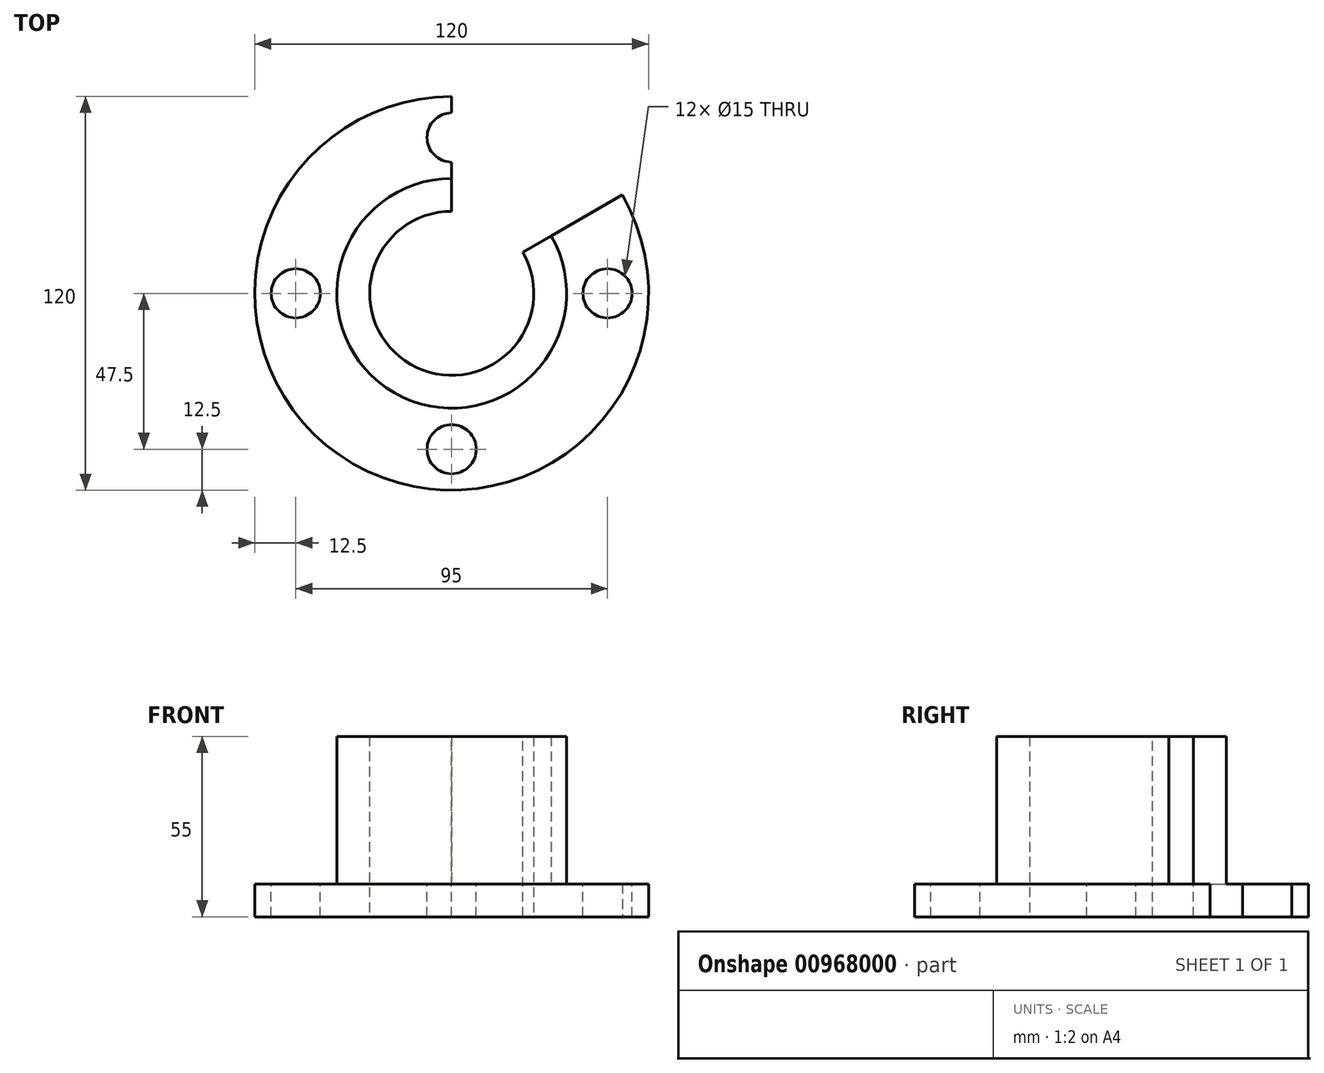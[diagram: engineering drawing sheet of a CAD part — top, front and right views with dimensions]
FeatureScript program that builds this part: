
annotation { "Feature Type Name" : "Feature", "Feature Type Description" : "" }
export const myFeature = defineFeature(function(context is Context, id is Id, definition is map)
    precondition{}
    {
        {
            var Q0;
            Q0=qCreatedBy(makeId("Right.planeOp"),FACE);
            var sketch = newSketch(context, id + "F0", { "sketchPlane" : qUnion([Q0])});
            skLineSegment(sketch, "E0", {"start": v(0, 0) * mm, "end": v(0, 50.5) * mm});
            skLineSegment(sketch, "E1", {"start": v(25, 0) * mm, "end": v(25, 55) * mm});
            skLineSegment(sketch, "E2", {"start": v(25, 55) * mm, "end": v(35, 55) * mm});
            skLineSegment(sketch, "E3", {"start": v(35, 55) * mm, "end": v(35, 10) * mm});
            skLineSegment(sketch, "E4", {"start": v(35, 10) * mm, "end": v(60, 10) * mm});
            skLineSegment(sketch, "E5", {"start": v(60, 10) * mm, "end": v(60, 0) * mm});
            skLineSegment(sketch, "E6", {"start": v(60, 0) * mm, "end": v(25, 0) * mm});
            skSolve(sketch);
        }
        {
            var Q0;
            Q0 = qSketchRegion(id + "F0", true);
            var Q1;
            Q1=sQuery(id+"F0.wireOp",EDGE,"E0");
            revolve(context, id + "F1", {"surfaceOperationType" : NewSurfaceOperationType.NEW, "entities" : qUnion([Q0]), "axis" : qUnion([Q1]), "revolveType" : RevolveType.ONE_DIRECTION, "angle" : 300 * degree});
        }
        {
            var Q0;
            Q0=makeQuery(id+"F1.opRevolve","SWEPT_FACE",FACE,{"disambiguationData":[OSD([sQuery(id+"F0.wireOp",EDGE,"E4")])]});
            var sketch = newSketch(context, id + "F2", { "sketchPlane" : qUnion([Q0])});
            skCircle(sketch, "E7", {"center": v(-47.5, 0) * mm, "radius": 7.5 * mm});
            skCircle(sketch, "E8", {"center": v(47.5, 0) * mm, "radius": 7.5 * mm});
            skCircle(sketch, "E9", {"center": v(0, 47.5) * mm, "radius": 7.5 * mm});
            skCircle(sketch, "E10", {"center": v(0, -47.5) * mm, "radius": 7.5 * mm});
            skSolve(sketch);
        }
        {
            var Q0;
            Q0=makeQuery(id+"F2.imprint","IMPRINT",FACE,{"disambiguationData":[TD([[makeQuery(id+"F2.imprint","IMPRINT",EDGE,{"derivedFrom":sQuery(id+"F2.wireOp",EDGE,"E7")}),1.0]])]});
            var Q1;
            Q1=makeQuery(id+"F2.imprint","IMPRINT",FACE,{"disambiguationData":[TD([[makeQuery(id+"F2.imprint","IMPRINT",EDGE,{"derivedFrom":sQuery(id+"F2.wireOp",EDGE,"E8")}),1.0]])]});
            var Q2;
            {var subQ0=sQuery(id+"F2.wireOp",EDGE,"E9");var subQ1=makeQuery(id+"F1.opRevolve","CAP_EDGE",EDGE,{"disambiguationData":[OSD([sQuery(id+"F0.wireOp",EDGE,"E4")])],"isStart":true});var subQ2=makeQuery(id+"F2.imprint","INTERSECT",VERTEX,{"disambiguationData":[OD(0.0)],"derivedFrom":[subQ1,subQ0]});Q2=makeQuery(id+"F2.imprint","IMPRINT",FACE,{"disambiguationData":[TD([[makeQuery(id+"F2.imprint","IMPRINT",EDGE,{"disambiguationData":[TD([[subQ2,-1.0]])],"derivedFrom":subQ0}),1.0]])]});}
            var Q3;
            {var subQ0=sQuery(id+"F2.wireOp",EDGE,"E9");var subQ1=makeQuery(id+"F1.opRevolve","CAP_EDGE",EDGE,{"disambiguationData":[OSD([sQuery(id+"F0.wireOp",EDGE,"E4")])],"isStart":true});var subQ2=makeQuery(id+"F2.imprint","INTERSECT",VERTEX,{"disambiguationData":[OD(0.0)],"derivedFrom":[subQ1,subQ0]});Q3=makeQuery(id+"F2.imprint","IMPRINT",FACE,{"disambiguationData":[TD([[makeQuery(id+"F2.imprint","IMPRINT",EDGE,{"disambiguationData":[TD([[subQ2,1.0]])],"derivedFrom":subQ0}),1.0]])]});}
            var Q4;
            Q4=makeQuery(id+"F2.imprint","IMPRINT",FACE,{"disambiguationData":[TD([[makeQuery(id+"F2.imprint","IMPRINT",EDGE,{"derivedFrom":sQuery(id+"F2.wireOp",EDGE,"E10")}),1.0]])]});
            extrude(context, id + "F3", {"entities" : qUnion([Q0, Q1, Q2, Q3, Q4]), "operationType" : NewBodyOperationType.REMOVE, "endBound" : BoundingType.THROUGH_ALL, "oppositeDirection" : true, "depth" : -25 * mm, "offsetDistance" : 25 * mm});
        }
    });
